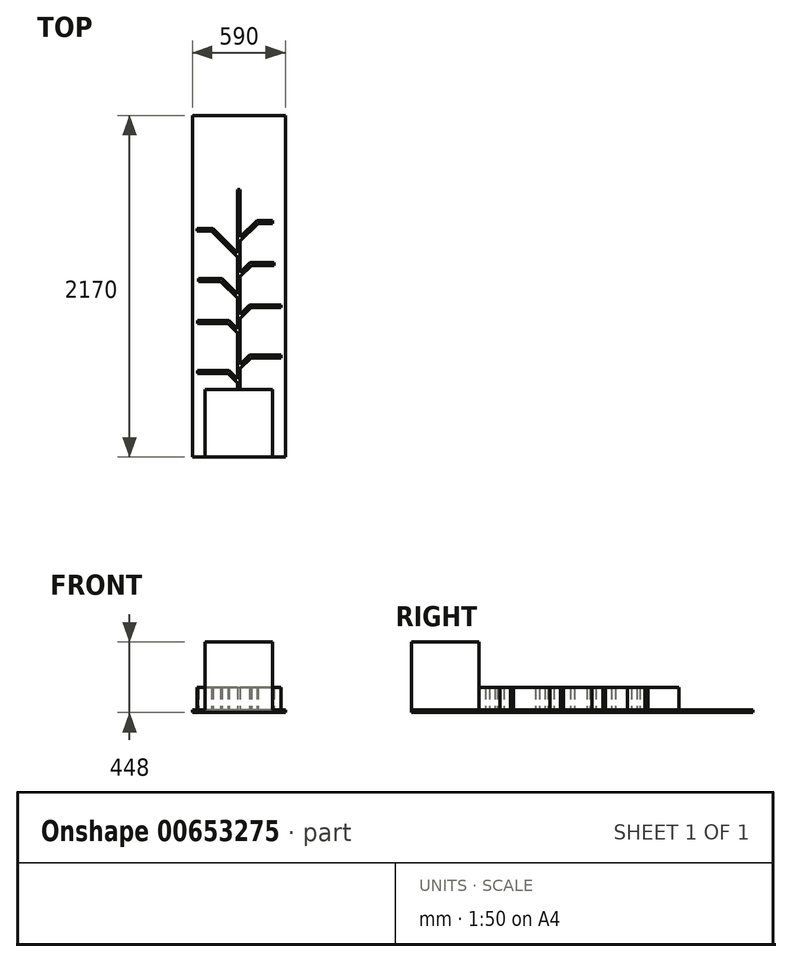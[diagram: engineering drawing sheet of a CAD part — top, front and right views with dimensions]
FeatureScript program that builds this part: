
annotation { "Feature Type Name" : "Feature", "Feature Type Description" : "" }
export const myFeature = defineFeature(function(context is Context, id is Id, definition is map)
    precondition{}
    {
        {
            var Q0;
            Q0=qCreatedBy(makeId("Top.planeOp"),FACE);
            var sketch = newSketch(context, id + "F0", { "sketchPlane" : qUnion([Q0])});
            skLineSegment(sketch, "E0.bottom", {"start": v(-294.29, -444.15) * mm, "end": v(295.71, -444.15) * mm});
            skLineSegment(sketch, "E0.top", {"start": v(-294.29, 1725.85) * mm, "end": v(295.71, 1725.85) * mm});
            skLineSegment(sketch, "E0.left", {"start": v(-294.29, -444.15) * mm, "end": v(-294.29, 1725.85) * mm});
            skLineSegment(sketch, "E0.right", {"start": v(295.71, -444.15) * mm, "end": v(295.71, 1725.85) * mm});
            skSolve(sketch);
        }
        {
            var Q0;
            Q0 = qSketchRegion(id + "F0", true);
            extrude(context, id + "F1", {"entities" : qUnion([Q0]), "depth" : 18 * mm, "offsetDistance" : 25 * mm});
        }
        {
            var Q0;
            Q0=makeQuery(id+"F1.opExtrude","CAP_FACE",FACE,{"disambiguationData":[OSD([sQuery(id+"F0.wireOp",EDGE,"E0.bottom"),sQuery(id+"F0.wireOp",EDGE,"E0.top"),sQuery(id+"F0.wireOp",EDGE,"E0.left"),sQuery(id+"F0.wireOp",EDGE,"E0.right")])],"isStart":false});
            var sketch = newSketch(context, id + "F2", { "sketchPlane" : qUnion([Q0])});
            skLineSegment(sketch, "E1.bottom", {"start": v(-9, -444.15) * mm, "end": v(9, -444.15) * mm});
            skLineSegment(sketch, "E1.top", {"start": v(-9, 1255.85) * mm, "end": v(9, 1255.85) * mm});
            skLineSegment(sketch, "E1.left", {"start": v(-9, -444.15) * mm, "end": v(-9, 1255.85) * mm});
            skLineSegment(sketch, "E1.right", {"start": v(9, -444.15) * mm, "end": v(9, 1255.85) * mm});
            skLineSegment(sketch, "E2", {"start": v(9, -14.15) * mm, "end": v(801.5, -14.15) * mm, "construction": true});
            skLineSegment(sketch, "E3", {"start": v(9, 436.3) * mm, "end": v(76.56, 503.85) * mm});
            skLineSegment(sketch, "E4", {"start": v(76.56, 503.85) * mm, "end": v(269.1, 503.85) * mm});
            skLineSegment(sketch, "E5", {"start": v(269.1, 503.85) * mm, "end": v(269.1, 521.85) * mm});
            skLineSegment(sketch, "E6", {"start": v(269.1, 521.85) * mm, "end": v(69.1, 521.85) * mm});
            skLineSegment(sketch, "E7", {"start": v(69.1, 521.85) * mm, "end": v(9, 461.75) * mm});
            skLineSegment(sketch, "E8", {"start": v(9, 461.75) * mm, "end": v(9, 436.3) * mm});
            skLineSegment(sketch, "E9", {"start": v(9, 701.14) * mm, "end": v(79.71, 771.85) * mm});
            skLineSegment(sketch, "E10", {"start": v(79.71, 771.85) * mm, "end": v(222.25, 771.85) * mm});
            skLineSegment(sketch, "E11", {"start": v(222.25, 771.85) * mm, "end": v(222.25, 789.85) * mm});
            skLineSegment(sketch, "E12", {"start": v(222.25, 789.85) * mm, "end": v(72.25, 789.85) * mm});
            skLineSegment(sketch, "E13", {"start": v(72.25, 789.85) * mm, "end": v(9, 726.6) * mm});
            skLineSegment(sketch, "E14", {"start": v(9, 726.6) * mm, "end": v(9, 701.14) * mm});
            skLineSegment(sketch, "E15", {"start": v(9, 926.71) * mm, "end": v(122.14, 1039.85) * mm});
            skLineSegment(sketch, "E16", {"start": v(122.14, 1039.85) * mm, "end": v(214.68, 1039.85) * mm});
            skLineSegment(sketch, "E17", {"start": v(214.68, 1039.85) * mm, "end": v(214.68, 1057.85) * mm});
            skLineSegment(sketch, "E18", {"start": v(214.68, 1057.85) * mm, "end": v(114.68, 1057.85) * mm});
            skLineSegment(sketch, "E19", {"start": v(114.68, 1057.85) * mm, "end": v(9, 952.17) * mm});
            skLineSegment(sketch, "E20", {"start": v(-9, 852.29) * mm, "end": v(-164.56, 1007.85) * mm});
            skLineSegment(sketch, "E21", {"start": v(-164.56, 1007.85) * mm, "end": v(-264.56, 1007.85) * mm});
            skLineSegment(sketch, "E22", {"start": v(-264.56, 1007.85) * mm, "end": v(-264.56, 989.85) * mm});
            skLineSegment(sketch, "E23", {"start": v(-264.56, 989.85) * mm, "end": v(-172.02, 989.85) * mm});
            skLineSegment(sketch, "E24", {"start": v(-172.02, 989.85) * mm, "end": v(-9, 826.83) * mm});
            skLineSegment(sketch, "E25", {"start": v(-9, 369.2) * mm, "end": v(-61.65, 421.85) * mm});
            skLineSegment(sketch, "E26", {"start": v(-61.65, 421.85) * mm, "end": v(-261.65, 421.85) * mm});
            skLineSegment(sketch, "E27", {"start": v(-261.65, 421.85) * mm, "end": v(-261.65, 403.85) * mm});
            skLineSegment(sketch, "E28", {"start": v(-261.65, 403.85) * mm, "end": v(-69.1, 403.85) * mm});
            skLineSegment(sketch, "E29", {"start": v(-69.1, 403.85) * mm, "end": v(-9, 343.75) * mm});
            skLineSegment(sketch, "E30", {"start": v(-61.65, 103.85) * mm, "end": v(-261.65, 103.85) * mm});
            skLineSegment(sketch, "E31", {"start": v(-261.65, 103.85) * mm, "end": v(-261.65, 85.85) * mm});
            skLineSegment(sketch, "E32", {"start": v(-261.65, 85.85) * mm, "end": v(-69.1, 85.85) * mm});
            skLineSegment(sketch, "E33", {"start": v(9, 118.3) * mm, "end": v(76.56, 185.85) * mm});
            skLineSegment(sketch, "E34", {"start": v(76.56, 185.85) * mm, "end": v(269.1, 185.85) * mm});
            skLineSegment(sketch, "E35", {"start": v(269.1, 185.85) * mm, "end": v(269.1, 203.85) * mm});
            skLineSegment(sketch, "E36", {"start": v(269.1, 203.85) * mm, "end": v(69.1, 203.85) * mm});
            skLineSegment(sketch, "E37", {"start": v(69.1, 203.85) * mm, "end": v(9, 143.75) * mm});
            skLineSegment(sketch, "E38", {"start": v(9, 143.75) * mm, "end": v(9, 118.3) * mm});
            skLineSegment(sketch, "E39", {"start": v(-61.65, 103.85) * mm, "end": v(-9, 51.2) * mm});
            skLineSegment(sketch, "E40", {"start": v(-69.1, 85.85) * mm, "end": v(-9, 25.75) * mm});
            skLineSegment(sketch, "E41", {"start": v(-9, 591.24) * mm, "end": v(-107.61, 689.85) * mm});
            skLineSegment(sketch, "E42", {"start": v(-107.61, 689.85) * mm, "end": v(-257.61, 689.85) * mm});
            skLineSegment(sketch, "E43", {"start": v(-257.61, 689.85) * mm, "end": v(-257.61, 671.85) * mm});
            skLineSegment(sketch, "E44", {"start": v(-257.61, 671.85) * mm, "end": v(-115.07, 671.85) * mm});
            skLineSegment(sketch, "E45", {"start": v(-115.07, 671.85) * mm, "end": v(-9, 565.78) * mm});
            skSolve(sketch);
        }
        {
            var Q0;
            Q0 = qSketchRegion(id + "F2", true);
            extrude(context, id + "F3", {"entities" : qUnion([Q0]), "operationType" : NewBodyOperationType.ADD, "depth" : 140 * mm, "offsetDistance" : 25 * mm});
        }
        {
            var Q0;
            Q0=makeQuery(id+"F1.opExtrude","CAP_FACE",FACE,{"disambiguationData":[OSD([sQuery(id+"F0.wireOp",EDGE,"E0.bottom"),sQuery(id+"F0.wireOp",EDGE,"E0.top"),sQuery(id+"F0.wireOp",EDGE,"E0.left"),sQuery(id+"F0.wireOp",EDGE,"E0.right")])],"isStart":false});
            var sketch = newSketch(context, id + "F4", { "sketchPlane" : qUnion([Q0])});
            skLineSegment(sketch, "E46.bottom", {"start": v(-215, -444.15) * mm, "end": v(215, -444.15) * mm});
            skLineSegment(sketch, "E46.top", {"start": v(-215, -14.15) * mm, "end": v(215, -14.15) * mm});
            skLineSegment(sketch, "E46.left", {"start": v(-215, -444.15) * mm, "end": v(-215, -14.15) * mm});
            skLineSegment(sketch, "E46.right", {"start": v(215, -444.15) * mm, "end": v(215, -14.15) * mm});
            skSolve(sketch);
        }
        {
            var Q0;
            Q0 = qSketchRegion(id + "F4", true);
            extrude(context, id + "F5", {"entities" : qUnion([Q0]), "operationType" : NewBodyOperationType.ADD, "depth" : 430 * mm, "offsetDistance" : 25 * mm});
        }
    });
